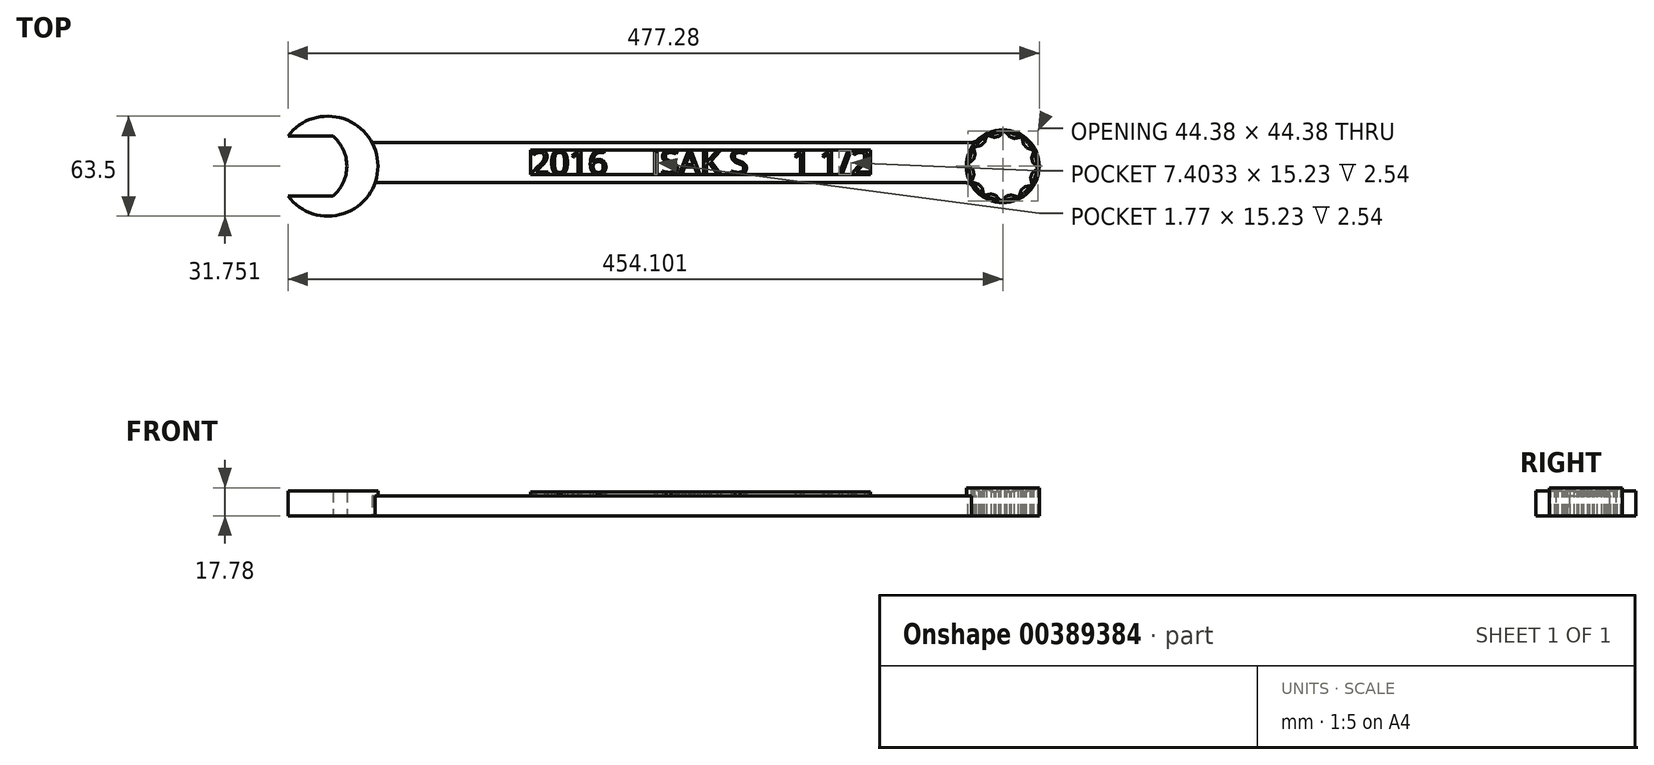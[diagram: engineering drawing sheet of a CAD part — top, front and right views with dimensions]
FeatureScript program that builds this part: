
annotation { "Feature Type Name" : "Feature", "Feature Type Description" : "" }
export const myFeature = defineFeature(function(context is Context, id is Id, definition is map)
    precondition{}
    {
        {
            var Q0;
            Q0=qCreatedBy(makeId("Top.planeOp"),FACE);
            var sketch = newSketch(context, id + "F0", { "sketchPlane" : qUnion([Q0])});
            skArc(sketch, "E0", {"start": v(-25.4, -41.95) * mm, "mid": v(31.75, -22.9) * mm, "end": v(-25.4, -3.85) * mm});
            skLineSegment(sketch, "E1", {"start": v(-25.4, -41.95) * mm, "end": v(3.18, -41.95) * mm});
            skLineSegment(sketch, "E2", {"start": v(28.02, -7.98) * mm, "end": v(408.03, -7.98) * mm});
            skLineSegment(sketch, "E3", {"start": v(404.63, -33.38) * mm, "end": v(29.97, -33.38) * mm});
            skCircle(sketch, "E4", {"center": v(428.7, -22.9) * mm, "radius": 22.23 * mm});
            skLineSegment(sketch, "E5", {"start": v(410.1, -7.63) * mm, "end": v(413.9, -6.32) * mm});
            skLineSegment(sketch, "E6", {"start": v(407.91, -34.3) * mm, "end": v(410.75, -36) * mm});
            skPoint(sketch, "E7.visualSharp", {"position": v(409.1, -7.98) * mm});
            skArc(sketch, "E7.filletArc", {"start": v(408.03, -7.98) * mm, "mid": v(409.08, -7.9) * mm, "end": v(410.1, -7.63) * mm});
            skPoint(sketch, "E8.visualSharp", {"position": v(406.4, -33.38) * mm});
            skArc(sketch, "E8.filletArc", {"start": v(407.91, -34.3) * mm, "mid": v(406.34, -33.61) * mm, "end": v(404.63, -33.38) * mm});
            skCircle(sketch, "E9", {"center": v(428.7, -22.9) * mm, "radius": 19.05 * mm});
            skLineSegment(sketch, "E10", {"start": v(250.87, -29.08) * mm, "end": v(144.28, -29.08) * mm});
            skLineSegment(sketch, "E11", {"start": v(144.28, -18.92) * mm, "end": v(250.77, -18.92) * mm});
            skLineSegment(sketch, "E12", {"start": v(253.95, -22.02) * mm, "end": v(254.04, -25.83) * mm});
            skLineSegment(sketch, "E13", {"start": v(141.1, -22.1) * mm, "end": v(141.1, -25.9) * mm});
            skPoint(sketch, "E14.visualSharp", {"position": v(141.1, -18.92) * mm});
            skArc(sketch, "E14.filletArc", {"start": v(144.28, -18.92) * mm, "mid": v(142.03, -19.85) * mm, "end": v(141.1, -22.1) * mm});
            skPoint(sketch, "E15.visualSharp", {"position": v(141.1, -29.08) * mm});
            skArc(sketch, "E15.filletArc", {"start": v(141.1, -25.9) * mm, "mid": v(142.03, -28.15) * mm, "end": v(144.28, -29.08) * mm});
            skPoint(sketch, "E16.visualSharp", {"position": v(253.87, -18.92) * mm});
            skArc(sketch, "E16.filletArc", {"start": v(253.95, -22.02) * mm, "mid": v(253, -19.83) * mm, "end": v(250.77, -18.92) * mm});
            skArc(sketch, "E17.filletArc", {"start": v(250.87, -29.08) * mm, "mid": v(253.14, -28.13) * mm, "end": v(254.04, -25.83) * mm});
            skText(sketch, "E18", { "text": "2016                         ISAK S                      1 1/2\"", "fontName": "OpenSans-Regular.ttf"});
            skLineSegment(sketch, "E19", {"start": v(-25.4, -3.85) * mm, "end": v(3.18, -3.85) * mm});
            skArc(sketch, "E20", {"start": v(3.18, -41.95) * mm, "mid": v(12.07, -22.9) * mm, "end": v(3.18, -3.85) * mm});
            const initialGuessF0  = {"E18": [0.14428, -0.0259, 1, 0, 0.00381]};
            skSetInitialGuess(sketch, initialGuessF0);
            skSolve(sketch);
        }
        {
            var Q0;
            {var subQ2=sQuery(id+"F0.wireOp",EDGE,"E2");Q0=makeQuery(id+"F0.imprint","IMPRINT",FACE,{"disambiguationData":[TD([[makeQuery(id+"F0.imprint","IMPRINT",EDGE,{"derivedFrom":subQ2}),-1.0]])]});}
            var Q1;
            Q1=makeQuery(id+"F0.imprint","IMPRINT",FACE,{"disambiguationData":[TD([[makeQuery(id+"F0.imprint","IMPRINT",EDGE,{"derivedFrom":sQuery(id+"F0.wireOp",EDGE,"E10")}),-1.0]])]});
            var Q2;
            Q2=makeQuery(id+"F0.imprint","IMPRINT",FACE,{"disambiguationData":[TD([[makeQuery(id+"F0.imprint","IMPRINT",EDGE,{"derivedFrom":sQuery(id+"F0.wireOp",EDGE,"E18.sketch_text.stroke-167")}),-1.0]])]});
            var Q3;
            Q3=makeQuery(id+"F0.imprint","IMPRINT",FACE,{"disambiguationData":[TD([[makeQuery(id+"F0.imprint","IMPRINT",EDGE,{"derivedFrom":sQuery(id+"F0.wireOp",EDGE,"E18.sketch_text.stroke-124")}),-1.0]])]});
            var Q4;
            Q4=makeQuery(id+"F0.imprint","IMPRINT",FACE,{"disambiguationData":[TD([[makeQuery(id+"F0.imprint","IMPRINT",EDGE,{"derivedFrom":sQuery(id+"F0.wireOp",EDGE,"E18.sketch_text.stroke-70")}),-1.0]])]});
            var Q5;
            Q5=makeQuery(id+"F0.imprint","IMPRINT",FACE,{"disambiguationData":[TD([[makeQuery(id+"F0.imprint","IMPRINT",EDGE,{"derivedFrom":sQuery(id+"F0.wireOp",EDGE,"E18.sketch_text.stroke-99")}),-1.0]])]});
            var Q6;
            Q6=makeQuery(id+"F0.imprint","IMPRINT",FACE,{"disambiguationData":[TD([[makeQuery(id+"F0.imprint","IMPRINT",EDGE,{"derivedFrom":sQuery(id+"F0.wireOp",EDGE,"E18.sketch_text.stroke-112")}),-1.0]])]});
            var Q7;
            Q7=makeQuery(id+"F0.imprint","IMPRINT",FACE,{"disambiguationData":[TD([[makeQuery(id+"F0.imprint","IMPRINT",EDGE,{"derivedFrom":sQuery(id+"F0.wireOp",EDGE,"E18.sketch_text.stroke-36")}),-1.0]])]});
            var Q8;
            Q8=makeQuery(id+"F0.imprint","IMPRINT",FACE,{"disambiguationData":[TD([[makeQuery(id+"F0.imprint","IMPRINT",EDGE,{"derivedFrom":sQuery(id+"F0.wireOp",EDGE,"E18.sketch_text.stroke-158")}),-1.0]])]});
            var Q9;
            Q9=makeQuery(id+"F0.imprint","IMPRINT",FACE,{"disambiguationData":[TD([[makeQuery(id+"F0.imprint","IMPRINT",EDGE,{"derivedFrom":sQuery(id+"F0.wireOp",EDGE,"E18.sketch_text.stroke-149")}),-1.0]])]});
            var Q10;
            Q10=makeQuery(id+"F0.imprint","IMPRINT",FACE,{"disambiguationData":[TD([[makeQuery(id+"F0.imprint","IMPRINT",EDGE,{"derivedFrom":sQuery(id+"F0.wireOp",EDGE,"E18.sketch_text.stroke-20")}),-1.0]])]});
            var Q11;
            Q11=makeQuery(id+"F0.imprint","IMPRINT",FACE,{"disambiguationData":[TD([[makeQuery(id+"F0.imprint","IMPRINT",EDGE,{"derivedFrom":sQuery(id+"F0.wireOp",EDGE,"E18.sketch_text.stroke-28")}),1.0]])]});
            var Q12;
            Q12=makeQuery(id+"F0.imprint","IMPRINT",FACE,{"disambiguationData":[TD([[makeQuery(id+"F0.imprint","IMPRINT",EDGE,{"derivedFrom":sQuery(id+"F0.wireOp",EDGE,"E18.sketch_text.stroke-45")}),-1.0]])]});
            var Q13;
            Q13=makeQuery(id+"F0.imprint","IMPRINT",FACE,{"disambiguationData":[TD([[makeQuery(id+"F0.imprint","IMPRINT",EDGE,{"derivedFrom":sQuery(id+"F0.wireOp",EDGE,"E18.sketch_text.stroke-74")}),-1.0]])]});
            var Q14;
            Q14=makeQuery(id+"F0.imprint","IMPRINT",FACE,{"disambiguationData":[TD([[makeQuery(id+"F0.imprint","IMPRINT",EDGE,{"derivedFrom":sQuery(id+"F0.wireOp",EDGE,"E18.sketch_text.stroke-60")}),1.0]])]});
            var Q15;
            Q15=makeQuery(id+"F0.imprint","IMPRINT",FACE,{"disambiguationData":[TD([[makeQuery(id+"F0.imprint","IMPRINT",EDGE,{"derivedFrom":sQuery(id+"F0.wireOp",EDGE,"E18.sketch_text.stroke-107")}),1.0]])]});
            var Q16;
            Q16=makeQuery(id+"F0.imprint","IMPRINT",FACE,{"disambiguationData":[TD([[makeQuery(id+"F0.imprint","IMPRINT",EDGE,{"derivedFrom":sQuery(id+"F0.wireOp",EDGE,"E18.sketch_text.stroke-171")}),-1.0]])]});
            var Q17;
            Q17=makeQuery(id+"F0.imprint","IMPRINT",FACE,{"disambiguationData":[TD([[makeQuery(id+"F0.imprint","IMPRINT",EDGE,{"derivedFrom":sQuery(id+"F0.wireOp",EDGE,"E18.sketch_text.stroke-0")}),-1.0]])]});
            var Q18;
            Q18=makeQuery(id+"F0.imprint","IMPRINT",FACE,{"disambiguationData":[TD([[makeQuery(id+"F0.imprint","IMPRINT",EDGE,{"derivedFrom":sQuery(id+"F0.wireOp",EDGE,"E18.sketch_text.stroke-195")}),-1.0]])]});
            var Q19;
            Q19=makeQuery(id+"F0.imprint","IMPRINT",FACE,{"disambiguationData":[TD([[makeQuery(id+"F0.imprint","IMPRINT",EDGE,{"derivedFrom":sQuery(id+"F0.wireOp",EDGE,"E18.sketch_text.stroke-191")}),-1.0]])]});
            extrude(context, id + "F1", {"entities" : qUnion([Q0, Q1, Q2, Q3, Q4, Q5, Q6, Q7, Q8, Q9, Q10, Q11, Q12, Q13, Q14, Q15, Q16, Q17, Q18, Q19]), "depth" : 12.7 * mm});
        }
        {
            var Q0;
            {var subQ0=sQuery(id+"F0.wireOp",EDGE,"E1");Q0=makeQuery(id+"F0.imprint","IMPRINT",FACE,{"disambiguationData":[TD([[makeQuery(id+"F0.imprint","IMPRINT",EDGE,{"derivedFrom":subQ0}),-1.0]])]});}
            extrude(context, id + "F2", {"entities" : qUnion([Q0]), "operationType" : NewBodyOperationType.ADD, "depth" : 15.88 * mm});
        }
        {
            var Q0;
            {var subQ0=sQuery(id+"F0.wireOp",EDGE,"E4");var subQ1=makeQuery(id+"F0.imprint","INTERSECT",VERTEX,{"derivedFrom":[subQ0,sQuery(id+"F0.wireOp",EDGE,"E5")]});Q0=makeQuery(id+"F0.imprint","IMPRINT",FACE,{"disambiguationData":[TD([[makeQuery(id+"F0.imprint","IMPRINT",EDGE,{"disambiguationData":[TD([[subQ1,-1.0]])],"derivedFrom":subQ0}),1.0]])]});}
            extrude(context, id + "F3", {"entities" : qUnion([Q0]), "operationType" : NewBodyOperationType.ADD, "depth" : 17.78 * mm});
        }
        {
            var Q0;
            Q0=makeQuery(id+"F3.opExtrude","CAP_EDGE",EDGE,{"disambiguationData":[OSD([sQuery(id+"F0.wireOp",EDGE,"E9")])],"isStart":false});
            chamfer(context, id + "F4", {"entities" : qUnion([Q0]), "width" : 2.54 * mm, "tangentPropagation" : true});
        }
        {
            var Q0;
            Q0=makeQuery(id+"F3.opExtrude","CAP_FACE",FACE,{"disambiguationData":[OSD([sQuery(id+"F0.wireOp",EDGE,"E4"),sQuery(id+"F0.wireOp",EDGE,"E9")])],"isStart":false});
            var sketch = newSketch(context, id + "F5", { "sketchPlane" : qUnion([Q0])});
            skLineSegment(sketch, "E21", {"start": v(410.63, -16.86) * mm, "end": v(409.3, -12.07) * mm});
            skLineSegment(sketch, "E22", {"start": v(409.3, -12.07) * mm, "end": v(414.08, -10.69) * mm});
            skLineSegment(sketch, "E23", {"start": v(414.08, -10.69) * mm, "end": v(414.58, -5.74) * mm});
            skLineSegment(sketch, "E24", {"start": v(414.58, -5.74) * mm, "end": v(419.54, -6.2) * mm});
            skLineSegment(sketch, "E25", {"start": v(419.54, -6.2) * mm, "end": v(421.81, -1.77) * mm});
            skLineSegment(sketch, "E26", {"start": v(421.81, -1.77) * mm, "end": v(426.19, -4.02) * mm});
            skLineSegment(sketch, "E27", {"start": v(426.19, -4.02) * mm, "end": v(429.9, -0.7) * mm});
            skLineSegment(sketch, "E28", {"start": v(429.9, -0.7) * mm, "end": v(433.18, -4.38) * mm});
            skLineSegment(sketch, "E29", {"start": v(433.18, -4.38) * mm, "end": v(437.84, -2.64) * mm});
            skLineSegment(sketch, "E30", {"start": v(437.84, -2.64) * mm, "end": v(439.56, -7.25) * mm});
            skLineSegment(sketch, "E31", {"start": v(450.9, -21.99) * mm, "end": v(447.55, -25.66) * mm});
            skLineSegment(sketch, "E32", {"start": v(410.63, -16.86) * mm, "end": v(406.68, -19.89) * mm});
            skLineSegment(sketch, "E33", {"start": v(439.56, -7.25) * mm, "end": v(444.48, -7.25) * mm});
            skLineSegment(sketch, "E34", {"start": v(449.09, -14.05) * mm, "end": v(447.26, -18.6) * mm});
            skLineSegment(sketch, "E35", {"start": v(447.26, -18.6) * mm, "end": v(450.9, -21.99) * mm});
            skLineSegment(sketch, "E36", {"start": v(445.28, -32.28) * mm, "end": v(445.68, -37.24) * mm});
            skLineSegment(sketch, "E37", {"start": v(447.55, -25.66) * mm, "end": v(449.7, -30.18) * mm});
            skLineSegment(sketch, "E38", {"start": v(449.7, -30.18) * mm, "end": v(445.28, -32.28) * mm});
            skLineSegment(sketch, "E39", {"start": v(445.68, -37.24) * mm, "end": v(440.77, -37.64) * mm});
            skLineSegment(sketch, "E40", {"start": v(440.77, -37.64) * mm, "end": v(439.38, -42.4) * mm});
            skLineSegment(sketch, "E41", {"start": v(439.38, -42.4) * mm, "end": v(434.68, -40.99) * mm});
            skLineSegment(sketch, "E42", {"start": v(434.68, -40.99) * mm, "end": v(431.67, -44.93) * mm});
            skLineSegment(sketch, "E43", {"start": v(431.67, -44.93) * mm, "end": v(427.75, -41.93) * mm});
            skLineSegment(sketch, "E44", {"start": v(427.75, -41.93) * mm, "end": v(423.53, -44.51) * mm});
            skLineSegment(sketch, "E45", {"start": v(423.53, -44.51) * mm, "end": v(420.83, -40.25) * mm});
            skLineSegment(sketch, "E46", {"start": v(420.83, -40.25) * mm, "end": v(415.97, -41.12) * mm});
            skLineSegment(sketch, "E47", {"start": v(415.97, -41.12) * mm, "end": v(415.08, -36.22) * mm});
            skLineSegment(sketch, "E48", {"start": v(415.08, -36.22) * mm, "end": v(410.21, -35.23) * mm});
            skLineSegment(sketch, "E49", {"start": v(410.21, -35.23) * mm, "end": v(411.18, -30.37) * mm});
            skLineSegment(sketch, "E50", {"start": v(411.18, -30.37) * mm, "end": v(407, -27.72) * mm});
            skLineSegment(sketch, "E51", {"start": v(407, -27.72) * mm, "end": v(409.66, -23.51) * mm});
            skLineSegment(sketch, "E52", {"start": v(409.66, -23.51) * mm, "end": v(406.68, -19.89) * mm});
            skCircle(sketch, "E53", {"center": v(428.7, -22.9) * mm, "radius": 23.18 * mm});
            skLineSegment(sketch, "E54", {"start": v(444.48, -12.23) * mm, "end": v(449.09, -14.05) * mm});
            skLineSegment(sketch, "E55", {"start": v(444.48, -7.25) * mm, "end": v(444.48, -12.23) * mm});
            skCircle(sketch, "E56", {"center": v(428.7, -22.9) * mm, "radius": 19.05 * mm});
            skSolve(sketch);
        }
        {
            var Q0;
            Q0=makeQuery(id+"F5.imprint","IMPRINT",FACE,{"disambiguationData":[TD([[makeQuery(id+"F5.imprint","IMPRINT",EDGE,{"derivedFrom":sQuery(id+"F5.wireOp",EDGE,"E53")}),1.0]])]});
            extrude(context, id + "F6", {"entities" : qUnion([Q0]), "operationType" : NewBodyOperationType.ADD, "oppositeDirection" : true, "depth" : 17.78 * mm});
        }
        {
            var Q0;
            {var subQ0=sQuery(id+"F5.wireOp",EDGE,"E27");Q0=makeQuery(id+"F5.imprint","IMPRINT",FACE,{"disambiguationData":[TD([[makeQuery(id+"F5.imprint","IMPRINT",EDGE,{"derivedFrom":subQ0}),-1.0]])]});}
            var Q1;
            {var subQ0=sQuery(id+"F5.wireOp",EDGE,"E56");var subQ1=sQuery(id+"F5.wireOp",EDGE,"E27");var subQ2=makeQuery(id+"F5.imprint","INTERSECT",VERTEX,{"derivedFrom":[sQuery(id+"F5.wireOp",EDGE,"E26"),subQ1,subQ0]});Q1=makeQuery(id+"F5.imprint","IMPRINT",FACE,{"disambiguationData":[TD([[makeQuery(id+"F5.imprint","IMPRINT",EDGE,{"disambiguationData":[TD([[subQ2,1.0]])],"derivedFrom":subQ0}),-1.0]])]});}
            var Q2;
            {var subQ0=sQuery(id+"F0.wireOp",EDGE,"E9");var subQ1=sQuery(id+"F0.wireOp",EDGE,"E4");var subQ2=sQuery(id+"F0.wireOp",EDGE,"E0");Q2=makeQuery(id+"F6.boolean.opBoolean","SPLIT",FACE,{"disambiguationData":[TD([makeQuery(id+"F3.opExtrude","SWEPT_FACE",FACE,{"disambiguationData":[OSD([subQ0])]})])],"derivedFrom":makeQuery(id+"F3.boolean.opBoolean","MERGE",FACE,{"derivedFrom":[makeQuery(id+"F2.boolean.opBoolean","MERGE",FACE,{"derivedFrom":[makeQuery(id+"F1.opExtrude","CAP_FACE",FACE,{"disambiguationData":[OSD([subQ2,sQuery(id+"F0.wireOp",EDGE,"E2"),sQuery(id+"F0.wireOp",EDGE,"E3"),subQ1,sQuery(id+"F0.wireOp",EDGE,"E5"),sQuery(id+"F0.wireOp",EDGE,"E6"),sQuery(id+"F0.wireOp",EDGE,"E7.filletArc"),sQuery(id+"F0.wireOp",EDGE,"E8.filletArc")])],"isStart":true}),makeQuery(id+"F2.opExtrude","CAP_FACE",FACE,{"disambiguationData":[OSD([subQ2,sQuery(id+"F0.wireOp",EDGE,"E1"),sQuery(id+"F0.wireOp",EDGE,"TriJaGZV-blu2-vSOX-xzdX-nboyACyyzU1x"),sQuery(id+"F0.wireOp",EDGE,"eWwwevlC-o9Po-upYn-ZwsQ-Ds7a017pBcme")])],"isStart":true})]}),makeQuery(id+"F3.opExtrude","CAP_FACE",FACE,{"disambiguationData":[OSD([subQ1,subQ0])],"isStart":true})]})});}
            extrude(context, id + "F7", {"entities" : qUnion([Q0, Q1]), "endBound" : BoundingType.UP_TO_SURFACE, "oppositeDirection" : true, "endBoundEntityFace" : qUnion([Q2]), "depth" : 25.4 * mm});
        }
        {
            var Q0;
            Q0=makeQuery(id+"F7.opExtrude","SWEPT_BODY",BODY,{"disambiguationData":[OSD([sQuery(id+"F0.wireOp",EDGE,"E9"),sQuery(id+"F5.wireOp",EDGE,"E27"),sQuery(id+"F5.wireOp",EDGE,"E28")])]});
            var Q1;
            Q1=makeQuery(id+"F3.opExtrude","SWEPT_FACE",FACE,{"disambiguationData":[OSD([sQuery(id+"F0.wireOp",EDGE,"E9")])]});
            circularPattern(context, id + "F8", {"entities" : qUnion([Q0]), "axis" : qUnion([Q1]), "angle" : 360 * degree, "instanceCount" : 12, "equalSpace" : true});
        }
        {
            var Q0;
            Q0=makeQuery(id+"F7.opExtrude","SWEPT_BODY",BODY,{"disambiguationData":[OSD([sQuery(id+"F0.wireOp",EDGE,"E9"),sQuery(id+"F5.wireOp",EDGE,"E27"),sQuery(id+"F5.wireOp",EDGE,"E28")])]});
            var Q1;
            Q1=makeQuery(id+"F8.opPattern","COPY",BODY,{"derivedFrom":makeQuery(id+"F7.opExtrude","SWEPT_BODY",BODY,{"disambiguationData":[OSD([sQuery(id+"F0.wireOp",EDGE,"E9"),sQuery(id+"F5.wireOp",EDGE,"E27"),sQuery(id+"F5.wireOp",EDGE,"E28")])]}),"instanceName":"1"});
            var Q2;
            Q2=makeQuery(id+"F8.opPattern","COPY",BODY,{"derivedFrom":makeQuery(id+"F7.opExtrude","SWEPT_BODY",BODY,{"disambiguationData":[OSD([sQuery(id+"F0.wireOp",EDGE,"E9"),sQuery(id+"F5.wireOp",EDGE,"E27"),sQuery(id+"F5.wireOp",EDGE,"E28")])]}),"instanceName":"2"});
            var Q3;
            Q3=makeQuery(id+"F8.opPattern","COPY",BODY,{"derivedFrom":makeQuery(id+"F7.opExtrude","SWEPT_BODY",BODY,{"disambiguationData":[OSD([sQuery(id+"F0.wireOp",EDGE,"E9"),sQuery(id+"F5.wireOp",EDGE,"E27"),sQuery(id+"F5.wireOp",EDGE,"E28")])]}),"instanceName":"3"});
            var Q4;
            Q4=makeQuery(id+"F8.opPattern","COPY",BODY,{"derivedFrom":makeQuery(id+"F7.opExtrude","SWEPT_BODY",BODY,{"disambiguationData":[OSD([sQuery(id+"F0.wireOp",EDGE,"E9"),sQuery(id+"F5.wireOp",EDGE,"E27"),sQuery(id+"F5.wireOp",EDGE,"E28")])]}),"instanceName":"4"});
            var Q5;
            Q5=makeQuery(id+"F8.opPattern","COPY",BODY,{"derivedFrom":makeQuery(id+"F7.opExtrude","SWEPT_BODY",BODY,{"disambiguationData":[OSD([sQuery(id+"F0.wireOp",EDGE,"E9"),sQuery(id+"F5.wireOp",EDGE,"E27"),sQuery(id+"F5.wireOp",EDGE,"E28")])]}),"instanceName":"5"});
            var Q6;
            Q6=makeQuery(id+"F8.opPattern","COPY",BODY,{"derivedFrom":makeQuery(id+"F7.opExtrude","SWEPT_BODY",BODY,{"disambiguationData":[OSD([sQuery(id+"F0.wireOp",EDGE,"E9"),sQuery(id+"F5.wireOp",EDGE,"E27"),sQuery(id+"F5.wireOp",EDGE,"E28")])]}),"instanceName":"6"});
            var Q7;
            Q7=makeQuery(id+"F8.opPattern","COPY",BODY,{"derivedFrom":makeQuery(id+"F7.opExtrude","SWEPT_BODY",BODY,{"disambiguationData":[OSD([sQuery(id+"F0.wireOp",EDGE,"E9"),sQuery(id+"F5.wireOp",EDGE,"E27"),sQuery(id+"F5.wireOp",EDGE,"E28")])]}),"instanceName":"7"});
            var Q8;
            Q8=makeQuery(id+"F8.opPattern","COPY",BODY,{"derivedFrom":makeQuery(id+"F7.opExtrude","SWEPT_BODY",BODY,{"disambiguationData":[OSD([sQuery(id+"F0.wireOp",EDGE,"E9"),sQuery(id+"F5.wireOp",EDGE,"E27"),sQuery(id+"F5.wireOp",EDGE,"E28")])]}),"instanceName":"8"});
            var Q9;
            Q9=makeQuery(id+"F8.opPattern","COPY",BODY,{"derivedFrom":makeQuery(id+"F7.opExtrude","SWEPT_BODY",BODY,{"disambiguationData":[OSD([sQuery(id+"F0.wireOp",EDGE,"E9"),sQuery(id+"F5.wireOp",EDGE,"E27"),sQuery(id+"F5.wireOp",EDGE,"E28")])]}),"instanceName":"9"});
            var Q10;
            Q10=makeQuery(id+"F8.opPattern","COPY",BODY,{"derivedFrom":makeQuery(id+"F7.opExtrude","SWEPT_BODY",BODY,{"disambiguationData":[OSD([sQuery(id+"F0.wireOp",EDGE,"E9"),sQuery(id+"F5.wireOp",EDGE,"E27"),sQuery(id+"F5.wireOp",EDGE,"E28")])]}),"instanceName":"10"});
            var Q11;
            Q11=makeQuery(id+"F8.opPattern","COPY",BODY,{"derivedFrom":makeQuery(id+"F7.opExtrude","SWEPT_BODY",BODY,{"disambiguationData":[OSD([sQuery(id+"F0.wireOp",EDGE,"E9"),sQuery(id+"F5.wireOp",EDGE,"E27"),sQuery(id+"F5.wireOp",EDGE,"E28")])]}),"instanceName":"11"});
            var Q12;
            Q12=makeQuery(id+"F1.opExtrude","SWEPT_BODY",BODY,{"disambiguationData":[OSD([sQuery(id+"F0.wireOp",EDGE,"E0"),sQuery(id+"F0.wireOp",EDGE,"E2"),sQuery(id+"F0.wireOp",EDGE,"E3"),sQuery(id+"F0.wireOp",EDGE,"E4"),sQuery(id+"F0.wireOp",EDGE,"E5"),sQuery(id+"F0.wireOp",EDGE,"E6"),sQuery(id+"F0.wireOp",EDGE,"E7.filletArc"),sQuery(id+"F0.wireOp",EDGE,"E8.filletArc")])]});
            booleanBodies(context, id + "F9", {"operationType" : BooleanOperationType.SUBTRACTION, "tools" : qUnion([Q0, Q1, Q2, Q3, Q4, Q5, Q6, Q7, Q8, Q9, Q10, Q11]), "targets" : qUnion([Q12])});
        }
        {
            var Q0;
            Q0=makeQuery(id+"F1.opExtrude","CAP_FACE",FACE,{"disambiguationData":[OSD([sQuery(id+"F0.wireOp",EDGE,"E0"),sQuery(id+"F0.wireOp",EDGE,"E2"),sQuery(id+"F0.wireOp",EDGE,"E3"),sQuery(id+"F0.wireOp",EDGE,"E4"),sQuery(id+"F0.wireOp",EDGE,"E5"),sQuery(id+"F0.wireOp",EDGE,"E6"),sQuery(id+"F0.wireOp",EDGE,"E7.filletArc"),sQuery(id+"F0.wireOp",EDGE,"E8.filletArc")])],"isStart":false});
            var sketch = newSketch(context, id + "F10", { "sketchPlane" : qUnion([Q0])});
            skPoint(sketch, "E57.endSnap0", {"position": v(31.66, -20.48) * mm});
            skLineSegment(sketch, "E58", {"start": v(128.85, -12.69) * mm, "end": v(344.75, -12.69) * mm});
            skLineSegment(sketch, "E59", {"start": v(344.75, -12.69) * mm, "end": v(344.75, -28.3) * mm});
            skLineSegment(sketch, "E60", {"start": v(344.75, -28.3) * mm, "end": v(128.85, -28.3) * mm});
            skLineSegment(sketch, "E61", {"start": v(128.85, -28.3) * mm, "end": v(128.85, -12.69) * mm});
            skLineSegment(sketch, "E62", {"start": v(128.85, -12.69) * mm, "end": v(128.85, -12.82) * mm});
            skLineSegment(sketch, "E63", {"start": v(128.85, -12.82) * mm, "end": v(344.75, -12.82) * mm});
            skPoint(sketch, "E63.endSnap0", {"position": v(344.75, -20.5) * mm});
            skLineSegment(sketch, "E64", {"start": v(128.85, -28.3) * mm, "end": v(128.85, -28.17) * mm});
            skLineSegment(sketch, "E65", {"start": v(128.85, -28.17) * mm, "end": v(344.75, -28.17) * mm});
            skText(sketch, "E66", { "text": "2016     ISAK S     1 1/2", "fontName": "OpenSans-Regular.ttf"});
            const initialGuessF10  = {"E66": [0.12885, -0.02817, 1, 0, 0.01536]};
            skSetInitialGuess(sketch, initialGuessF10);
            skSolve(sketch);
        }
        {
            var Q0;
            {var subQ0=sQuery(id+"F10.wireOp",EDGE,"E66.sketch_text.stroke-184");Q0=makeQuery(id+"F10.imprint","IMPRINT",FACE,{"disambiguationData":[TD([[makeQuery(id+"F10.imprint","IMPRINT",EDGE,{"derivedFrom":subQ0}),1.0]])]});}
            var Q1;
            Q1 = qSketchRegion(id + "F10", true);
            var Q2;
            {var subQ6=sQuery(id+"F10.wireOp",EDGE,"E66.sketch_text.stroke-13");Q2=makeQuery(id+"F10.imprint","IMPRINT",FACE,{"disambiguationData":[TD([[makeQuery(id+"F10.imprint","IMPRINT",EDGE,{"derivedFrom":subQ6}),1.0]])]});}
            var Q3;
            {var subQ1=sQuery(id+"F10.wireOp",EDGE,"E66.sketch_text.stroke-20");Q3=makeQuery(id+"F10.imprint","IMPRINT",FACE,{"disambiguationData":[TD([[makeQuery(id+"F10.imprint","IMPRINT",EDGE,{"derivedFrom":subQ1}),1.0]])]});}
            var Q4;
            {var subQ15=sQuery(id+"F10.wireOp",EDGE,"E66.sketch_text.stroke-48");Q4=makeQuery(id+"F10.imprint","IMPRINT",FACE,{"disambiguationData":[TD([[makeQuery(id+"F10.imprint","IMPRINT",EDGE,{"derivedFrom":subQ15}),1.0]])]});}
            var Q5;
            {var subQ16=sQuery(id+"F10.wireOp",EDGE,"E66.sketch_text.stroke-74");Q5=makeQuery(id+"F10.imprint","IMPRINT",FACE,{"disambiguationData":[TD([[makeQuery(id+"F10.imprint","IMPRINT",EDGE,{"derivedFrom":subQ16}),1.0]])]});}
            var Q6;
            Q6=makeQuery(id+"F10.imprint","IMPRINT",FACE,{"disambiguationData":[TD([[makeQuery(id+"F10.imprint","IMPRINT",EDGE,{"derivedFrom":sQuery(id+"F10.wireOp",EDGE,"E66.sketch_text.stroke-107")}),1.0]])]});
            var Q7;
            {var subQ0=sQuery(id+"F10.wireOp",EDGE,"E66.sketch_text.stroke-99");Q7=makeQuery(id+"F10.imprint","IMPRINT",FACE,{"disambiguationData":[TD([[makeQuery(id+"F10.imprint","IMPRINT",EDGE,{"derivedFrom":subQ0}),1.0]])]});}
            var Q8;
            {var subQ0=sQuery(id+"F10.wireOp",EDGE,"E66.sketch_text.stroke-113");Q8=makeQuery(id+"F10.imprint","IMPRINT",FACE,{"disambiguationData":[TD([[makeQuery(id+"F10.imprint","IMPRINT",EDGE,{"derivedFrom":subQ0}),1.0]])]});}
            var Q9;
            {var subQ18=sQuery(id+"F10.wireOp",EDGE,"E66.sketch_text.stroke-124");Q9=makeQuery(id+"F10.imprint","IMPRINT",FACE,{"disambiguationData":[TD([[makeQuery(id+"F10.imprint","IMPRINT",EDGE,{"derivedFrom":subQ18}),1.0]])]});}
            var Q10;
            Q10=makeQuery(id+"F10.imprint","IMPRINT",FACE,{"disambiguationData":[TD([[makeQuery(id+"F10.imprint","IMPRINT",EDGE,{"derivedFrom":sQuery(id+"F10.wireOp",EDGE,"E66.sketch_text.stroke-28")}),1.0]])]});
            var Q11;
            Q11=makeQuery(id+"F10.imprint","IMPRINT",FACE,{"disambiguationData":[TD([[makeQuery(id+"F10.imprint","IMPRINT",EDGE,{"derivedFrom":sQuery(id+"F10.wireOp",EDGE,"E66.sketch_text.stroke-60")}),1.0]])]});
            extrude(context, id + "F11", {"entities" : qUnion([Q0, Q1, Q2, Q3, Q4, Q5, Q6, Q7, Q8, Q9, Q10, Q11]), "operationType" : NewBodyOperationType.ADD, "depth" : 2.54 * mm});
        }
    });
